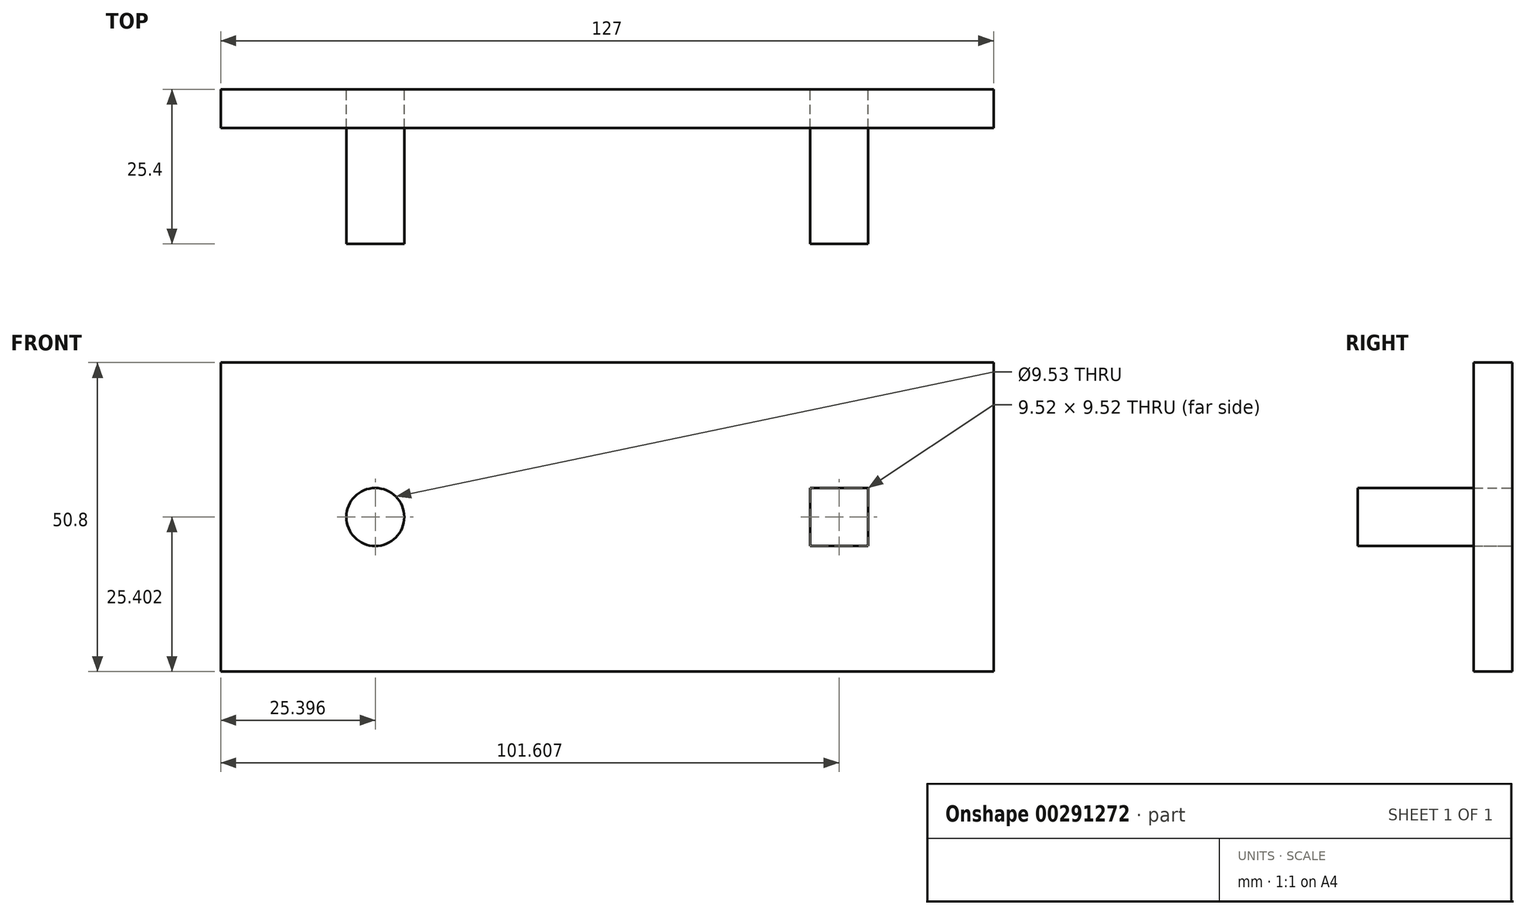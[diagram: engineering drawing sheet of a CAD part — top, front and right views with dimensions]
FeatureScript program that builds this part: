
annotation { "Feature Type Name" : "Feature", "Feature Type Description" : "" }
export const myFeature = defineFeature(function(context is Context, id is Id, definition is map)
    precondition{}
    {
        {
            var Q0;
            Q0=qCreatedBy(makeId("Front.planeOp"),FACE);
            var sketch = newSketch(context, id + "F0", { "sketchPlane" : qUnion([Q0])});
            skLineSegment(sketch, "E0.bottom", {"start": v(-138.21, 69.25) * mm, "end": v(-11.21, 69.25) * mm});
            skLineSegment(sketch, "E0.top", {"start": v(-138.21, 18.45) * mm, "end": v(-11.21, 18.45) * mm});
            skLineSegment(sketch, "E0.left", {"start": v(-138.21, 69.25) * mm, "end": v(-138.21, 18.45) * mm});
            skLineSegment(sketch, "E0.right", {"start": v(-11.21, 69.25) * mm, "end": v(-11.21, 18.45) * mm});
            skCircle(sketch, "E1", {"center": v(-112.81, 43.85) * mm, "radius": 4.76 * mm});
            skPoint(sketch, "E2.middle", {"position": v(-36.6, 43.85) * mm});
            skLineSegment(sketch, "E3.bottom", {"start": v(-31.84, 48.61) * mm, "end": v(-41.37, 48.61) * mm});
            skLineSegment(sketch, "E3.top", {"start": v(-31.84, 39.09) * mm, "end": v(-41.37, 39.09) * mm});
            skLineSegment(sketch, "E3.left", {"start": v(-31.84, 48.61) * mm, "end": v(-31.84, 39.09) * mm});
            skLineSegment(sketch, "E3.right", {"start": v(-41.37, 48.61) * mm, "end": v(-41.37, 39.09) * mm});
            skSolve(sketch);
        }
        {
            var Q0;
            Q0=makeQuery(id+"F0.imprint","IMPRINT",FACE,{"disambiguationData":[TD([[makeQuery(id+"F0.imprint","IMPRINT",EDGE,{"derivedFrom":sQuery(id+"F0.wireOp",EDGE,"E1")}),1.0]])]});
            var Q1;
            Q1=makeQuery(id+"F0.imprint","IMPRINT",FACE,{"disambiguationData":[TD([[makeQuery(id+"F0.imprint","IMPRINT",EDGE,{"derivedFrom":sQuery(id+"F0.wireOp",EDGE,"E3.bottom")}),1.0]])]});
            extrude(context, id + "F1", {"entities" : qUnion([Q0, Q1]), "depth" : 25.4 * mm});
        }
        {
            var Q0;
            Q0=makeQuery(id+"F0.imprint","IMPRINT",FACE,{"disambiguationData":[TD([[makeQuery(id+"F0.imprint","IMPRINT",EDGE,{"derivedFrom":sQuery(id+"F0.wireOp",EDGE,"E0.bottom")}),-1.0]])]});
            extrude(context, id + "F2", {"entities" : qUnion([Q0]), "depth" : 6.35 * mm});
        }
    });
